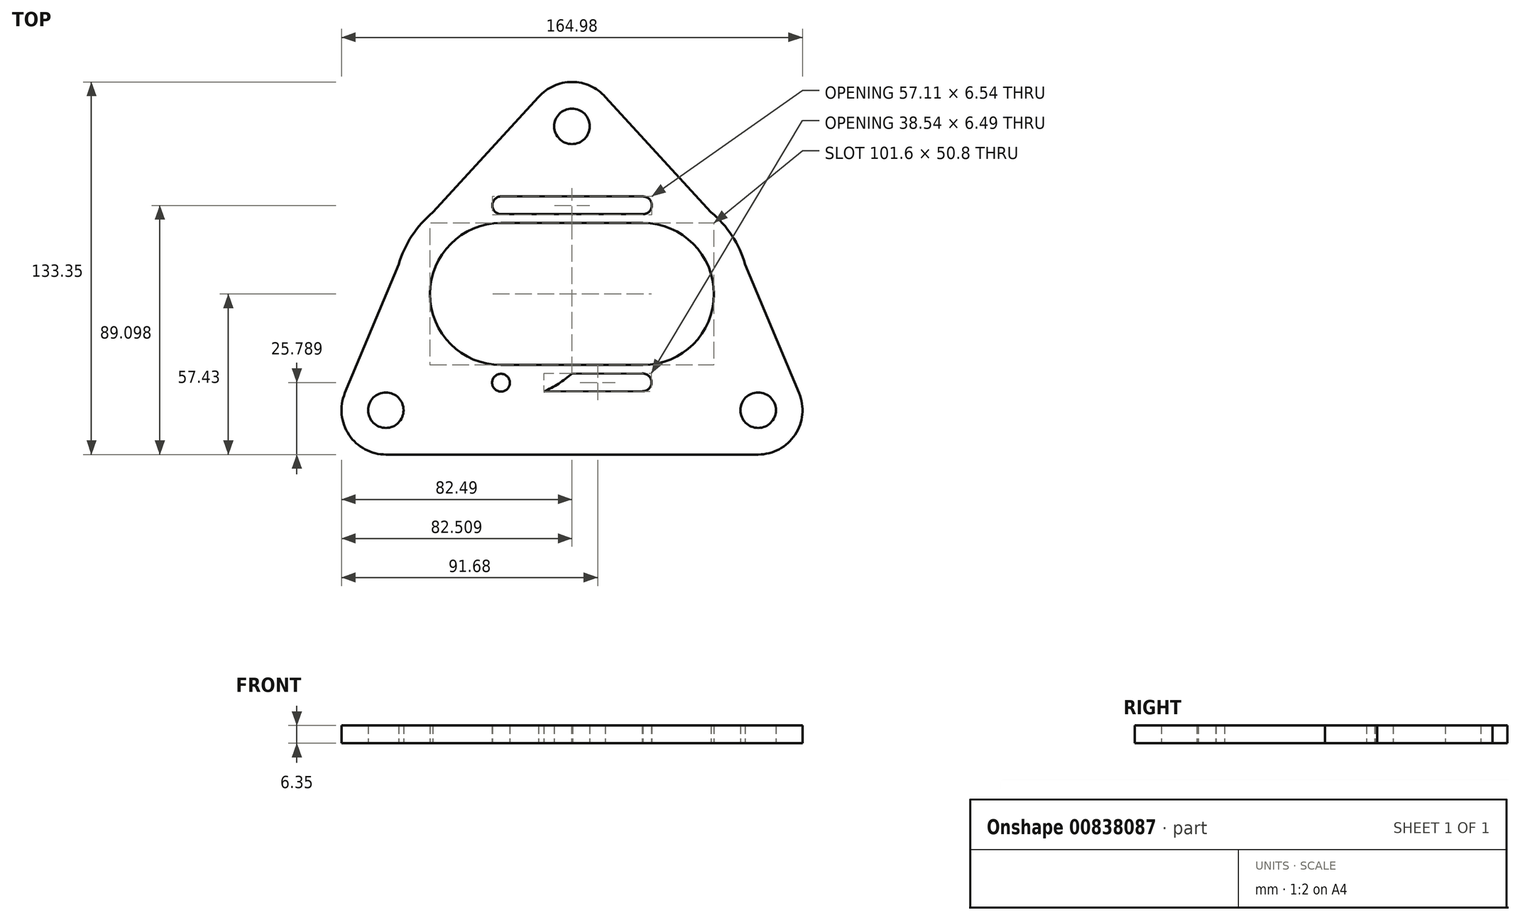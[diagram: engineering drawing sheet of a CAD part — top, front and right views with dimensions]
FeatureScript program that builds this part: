
annotation { "Feature Type Name" : "Feature", "Feature Type Description" : "" }
export const myFeature = defineFeature(function(context is Context, id is Id, definition is map)
    precondition{}
    {
        {
            var Q0;
            Q0=qCreatedBy(makeId("Top.planeOp"),FACE);
            var sketch = newSketch(context, id + "F0", { "sketchPlane" : qUnion([Q0])});
            skCircle(sketch, "E0", {"center": v(0, 60.04) * mm, "radius": 6.35 * mm});
            skCircle(sketch, "E1", {"center": v(-66.62, -41.56) * mm, "radius": 6.35 * mm});
            skCircle(sketch, "E2", {"center": v(0, 60.04) * mm, "radius": 15.88 * mm});
            skCircle(sketch, "E3", {"center": v(-66.62, -41.56) * mm, "radius": 15.88 * mm});
            skCircle(sketch, "E4", {"center": v(-25.4, 0) * mm, "radius": 25.4 * mm});
            skCircle(sketch, "E5", {"center": v(-25.4, 0) * mm, "radius": 38.1 * mm});
            skLineSegment(sketch, "E6", {"start": v(-61.98, 10.64) * mm, "end": v(-81.26, -35.43) * mm});
            skLineSegment(sketch, "E7", {"start": v(-11.43, 71.06) * mm, "end": v(-49.78, 29.28) * mm});
            skCircle(sketch, "E8.MirrorC", {"center": v(66.62, -41.56) * mm, "radius": 15.88 * mm});
            skCircle(sketch, "E9.MirrorC", {"center": v(25.4, 0) * mm, "radius": 38.1 * mm});
            skLineSegment(sketch, "E10.MirrorCS", {"start": v(11.43, 71.06) * mm, "end": v(49.78, 29.28) * mm});
            skCircle(sketch, "E11.MirrorC", {"center": v(66.62, -41.56) * mm, "radius": 6.35 * mm});
            skLineSegment(sketch, "E12.MirrorCS", {"start": v(61.98, 10.64) * mm, "end": v(81.26, -35.43) * mm});
            skCircle(sketch, "E13.MirrorC", {"center": v(25.4, 0) * mm, "radius": 25.4 * mm});
            skLineSegment(sketch, "E14", {"start": v(-66.7, -57.43) * mm, "end": v(66.62, -57.43) * mm});
            skLineSegment(sketch, "E15", {"start": v(25.4, 25.4) * mm, "end": v(-25.4, 25.4) * mm});
            skLineSegment(sketch, "E16", {"start": v(25.4, -25.4) * mm, "end": v(-25.4, -25.4) * mm});
            skLineSegment(sketch, "E17", {"start": v(25.4, 0) * mm, "end": v(25.4, 31.75) * mm, "construction": true});
            skLineSegment(sketch, "E18", {"start": v(-25.4, 0) * mm, "end": v(-25.4, 31.75) * mm, "construction": true});
            skLineSegment(sketch, "E19", {"start": v(25.4, 0) * mm, "end": v(25.4, -31.75) * mm, "construction": true});
            skLineSegment(sketch, "E20", {"start": v(25.4, -31.75) * mm, "end": v(-25.4, -31.75) * mm, "construction": true});
            skLineSegment(sketch, "E21", {"start": v(-25.4, -31.75) * mm, "end": v(-25.4, 0) * mm, "construction": true});
            skCircle(sketch, "E22", {"center": v(25.4, 31.75) * mm, "radius": 3.18 * mm});
            skCircle(sketch, "E23", {"center": v(-25.36, 31.76) * mm, "radius": 3.18 * mm});
            skCircle(sketch, "E24", {"center": v(25.29, -31.61) * mm, "radius": 3.18 * mm});
            skCircle(sketch, "E25", {"center": v(-25.4, -31.75) * mm, "radius": 3.18 * mm});
            skLineSegment(sketch, "E26", {"start": v(25.32, 34.92) * mm, "end": v(-25.36, 34.94) * mm});
            skLineSegment(sketch, "E27", {"start": v(25.4, 28.57) * mm, "end": v(-25.4, 28.59) * mm});
            skLineSegment(sketch, "E28", {"start": v(25.4, -28.44) * mm, "end": v(-25.4, -28.57) * mm});
            skLineSegment(sketch, "E29", {"start": v(25.28, -34.79) * mm, "end": v(-25.4, -34.92) * mm});
            skSolve(sketch);
        }
        {
            var Q0;
            Q0 = qSketchRegion(id + "F0", true);
            var Q1;
            {var subQ0=sQuery(id+"F0.wireOp",EDGE,"E9.MirrorC");var subQ1=sQuery(id+"F0.wireOp",EDGE,"E5");var subQ2=makeQuery(id+"F0.imprint","INTERSECT",VERTEX,{"disambiguationData":[OD(1.0)],"derivedFrom":[subQ1,subQ0]});Q1=makeQuery(id+"F0.imprint","IMPRINT",FACE,{"disambiguationData":[TD([[makeQuery(id+"F0.imprint","IMPRINT",EDGE,{"disambiguationData":[TD([[subQ2,-1.0]])],"derivedFrom":subQ1}),1.0]])]});}
            var Q2;
            {var subQ0=sQuery(id+"F0.wireOp",EDGE,"E15");var subQ1=sQuery(id+"F0.wireOp",EDGE,"E5");var subQ2=makeQuery(id+"F0.imprint","INTERSECT",VERTEX,{"derivedFrom":[subQ1,subQ0]});Q2=makeQuery(id+"F0.imprint","IMPRINT",FACE,{"disambiguationData":[TD([[makeQuery(id+"F0.imprint","IMPRINT",EDGE,{"disambiguationData":[TD([[subQ2,-1.0]])],"derivedFrom":subQ1}),1.0]])]});}
            extrude(context, id + "F1", {"entities" : qUnion([Q0, Q1, Q2]), "depth" : 6.35 * mm, "offsetDistance" : 25.4 * mm});
        }
    });
